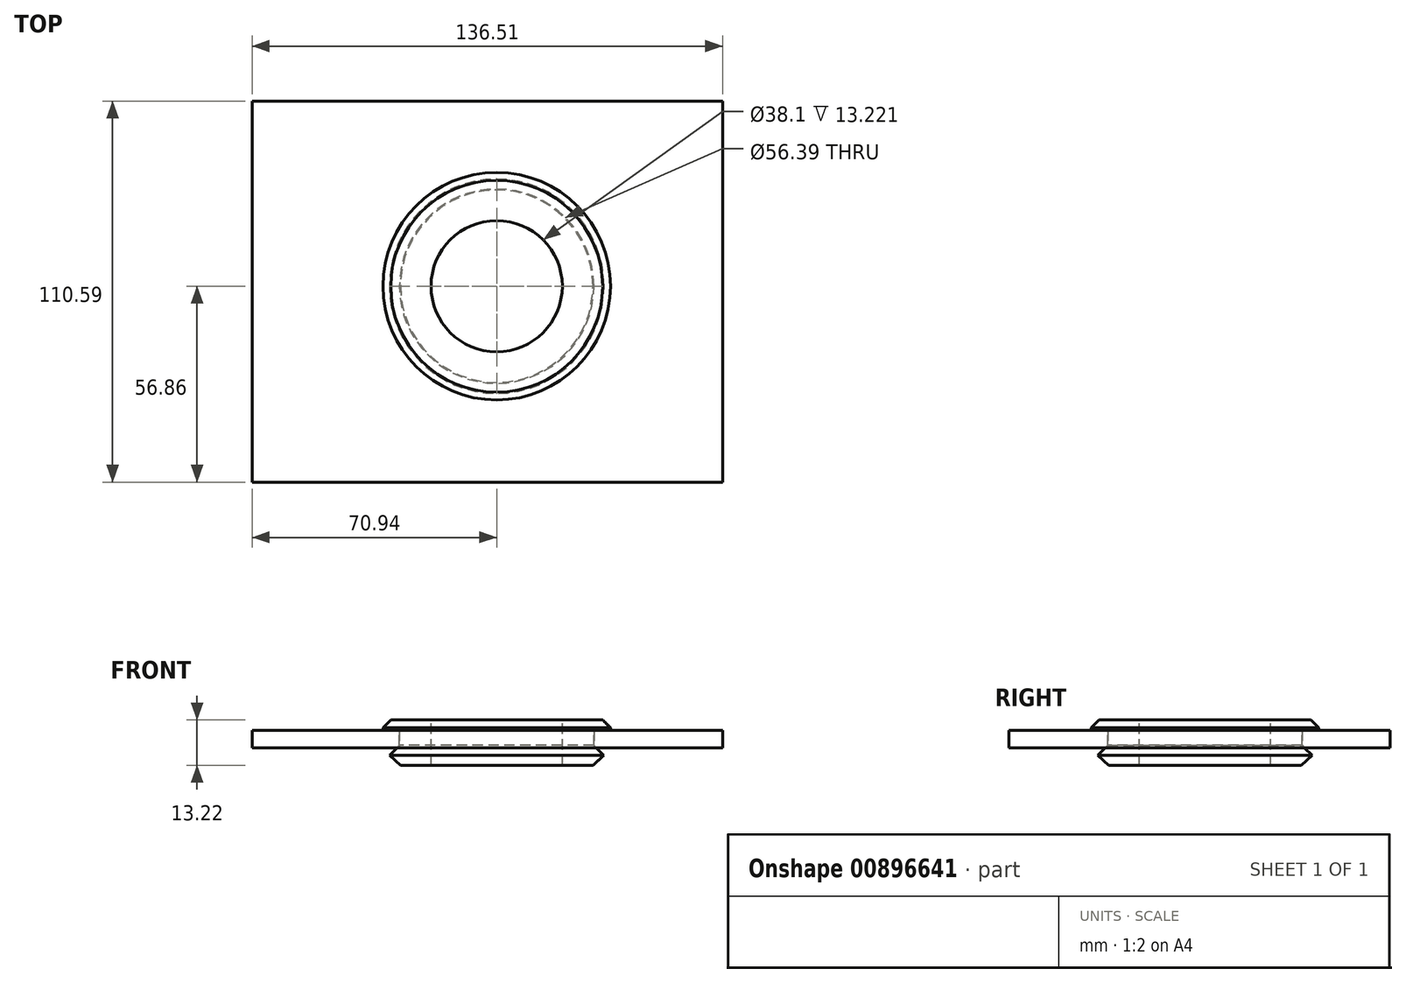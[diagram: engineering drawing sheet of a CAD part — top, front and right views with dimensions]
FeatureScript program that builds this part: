
annotation { "Feature Type Name" : "Feature", "Feature Type Description" : "" }
export const myFeature = defineFeature(function(context is Context, id is Id, definition is map)
    precondition{}
    {
        {
            var Q0;
            Q0=qCreatedBy(makeId("Top.planeOp"),FACE);
            var sketch = newSketch(context, id + "F0", { "sketchPlane" : qUnion([Q0])});
            skLineSegment(sketch, "E0.bottom", {"start": v(-70.94, -56.86) * mm, "end": v(65.57, -56.86) * mm});
            skLineSegment(sketch, "E0.top", {"start": v(-70.94, 53.73) * mm, "end": v(65.57, 53.73) * mm});
            skLineSegment(sketch, "E0.left", {"start": v(-70.94, -56.86) * mm, "end": v(-70.94, 53.73) * mm});
            skLineSegment(sketch, "E0.right", {"start": v(65.57, -56.86) * mm, "end": v(65.57, 53.73) * mm});
            skCircle(sketch, "E1", {"center": v(0, 0) * mm, "radius": 28.2 * mm});
            skSolve(sketch);
        }
        {
            var Q0;
            Q0=makeQuery(id+"F0.imprint","IMPRINT",FACE,{"disambiguationData":[TD([[makeQuery(id+"F0.imprint","IMPRINT",EDGE,{"derivedFrom":sQuery(id+"F0.wireOp",EDGE,"E0.bottom")}),1.0]])]});
            extrude(context, id + "F1", {"entities" : qUnion([Q0]), "depth" : 5.08 * mm, "offsetDistance" : 25.4 * mm});
        }
        {
            var Q0;
            Q0=qCreatedBy(makeId("Front.planeOp"),FACE);
            var sketch = newSketch(context, id + "F2", { "sketchPlane" : qUnion([Q0])});
            skLineSegment(sketch, "E2.0", {"start": v(-28.2, 5.08) * mm, "end": v(28.2, 5.08) * mm, "construction": true});
            skLineSegment(sketch, "E3.0", {"start": v(-28.2, 0) * mm, "end": v(28.2, 0) * mm, "construction": true});
            skLineSegment(sketch, "E4", {"start": v(0, 15.79) * mm, "end": v(0, -33.69) * mm, "construction": true});
            skLineSegment(sketch, "E5", {"start": v(19.05, 8.13) * mm, "end": v(30.73, 8.13) * mm});
            skLineSegment(sketch, "E6", {"start": v(30.73, 8.13) * mm, "end": v(33.02, 5.84) * mm});
            skLineSegment(sketch, "E7", {"start": v(33.02, 5.84) * mm, "end": v(33.02, 5.08) * mm});
            skLineSegment(sketch, "E8", {"start": v(33.02, 5.08) * mm, "end": v(28.2, 5.08) * mm});
            skLineSegment(sketch, "E9", {"start": v(28.2, 5.08) * mm, "end": v(28.2, 0.69) * mm});
            skLineSegment(sketch, "E10", {"start": v(28.2, 0.69) * mm, "end": v(31.12, -2.23) * mm});
            skLineSegment(sketch, "E11", {"start": v(31.12, -2.23) * mm, "end": v(27.94, -5.1) * mm});
            skLineSegment(sketch, "E12", {"start": v(19.05, 8.13) * mm, "end": v(19.05, -5.1) * mm});
            skLineSegment(sketch, "E13", {"start": v(19.05, -5.1) * mm, "end": v(27.94, -5.1) * mm});
            skSolve(sketch);
        }
        {
            var Q0;
            Q0=makeQuery(id+"F2.imprint","IMPRINT",FACE,{"disambiguationData":[TD([[makeQuery(id+"F2.imprint","IMPRINT",EDGE,{"derivedFrom":sQuery(id+"F2.wireOp",EDGE,"E5")}),-1.0]])]});
            var Q1;
            Q1=sQuery(id+"F2.wireOp",EDGE,"E4");
            revolve(context, id + "F3", {"surfaceOperationType" : NewSurfaceOperationType.NEW, "entities" : qUnion([Q0]), "axis" : qUnion([Q1]), "revolveType" : RevolveType.FULL});
        }
    });
